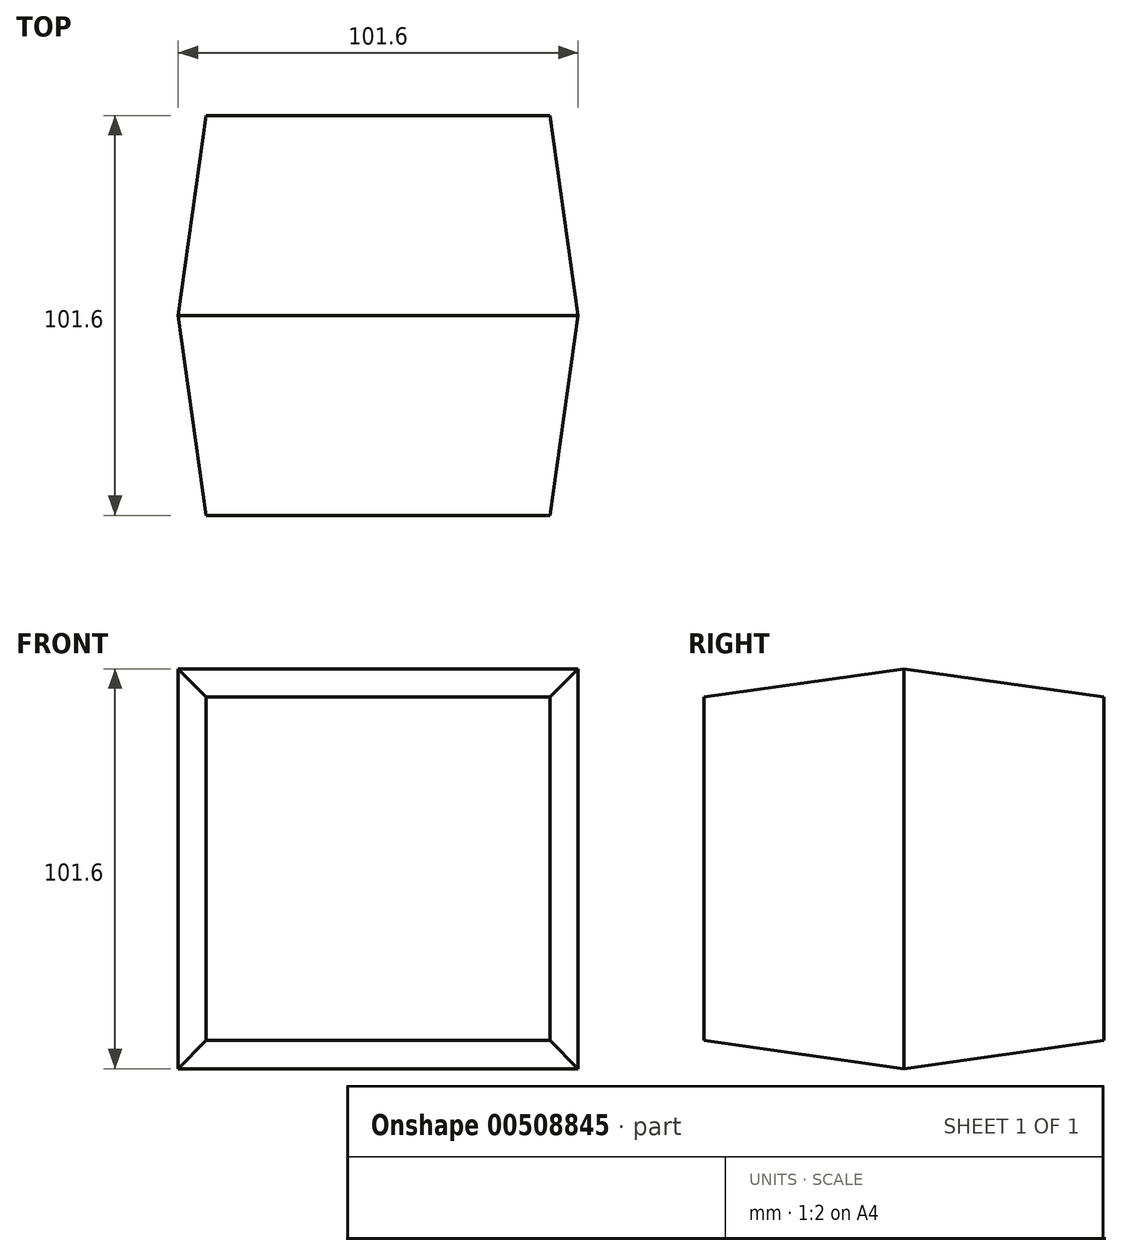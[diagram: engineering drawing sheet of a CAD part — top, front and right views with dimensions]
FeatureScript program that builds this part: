
annotation { "Feature Type Name" : "Feature", "Feature Type Description" : "" }
export const myFeature = defineFeature(function(context is Context, id is Id, definition is map)
    precondition{}
    {
        {
            var Q0;
            Q0=qCreatedBy(makeId("Front.planeOp"),FACE);
            var sketch = newSketch(context, id + "F0", { "sketchPlane" : qUnion([Q0])});
            skLineSegment(sketch, "E0.bottom", {"start": v(50.8, 50.8) * mm, "end": v(-50.8, 50.8) * mm});
            skLineSegment(sketch, "E0.top", {"start": v(50.8, -50.8) * mm, "end": v(-50.8, -50.8) * mm});
            skLineSegment(sketch, "E0.left", {"start": v(50.8, 50.8) * mm, "end": v(50.8, -50.8) * mm});
            skLineSegment(sketch, "E0.right", {"start": v(-50.8, 50.8) * mm, "end": v(-50.8, -50.8) * mm});
            skPoint(sketch, "E0.middle", {"position": v(0, 0) * mm});
            skSolve(sketch);
        }
        {
            var Q0;
            Q0=makeQuery(id+"F0.imprint","IMPRINT",FACE,{"disambiguationData":[TD([[makeQuery(id+"F0.imprint","IMPRINT",EDGE,{"derivedFrom":sQuery(id+"F0.wireOp",EDGE,"E0.bottom")}),1.0]])]});
            extrude(context, id + "F1", {"entities" : qUnion([Q0]), "endBound" : BoundingType.SYMMETRIC, "depth" : 101.6 * mm, "offsetDistance" : 25.4 * mm, "hasDraft" : true, "draftAngle" : 8 * degree, "draftPullDirection" : true});
        }
    });
